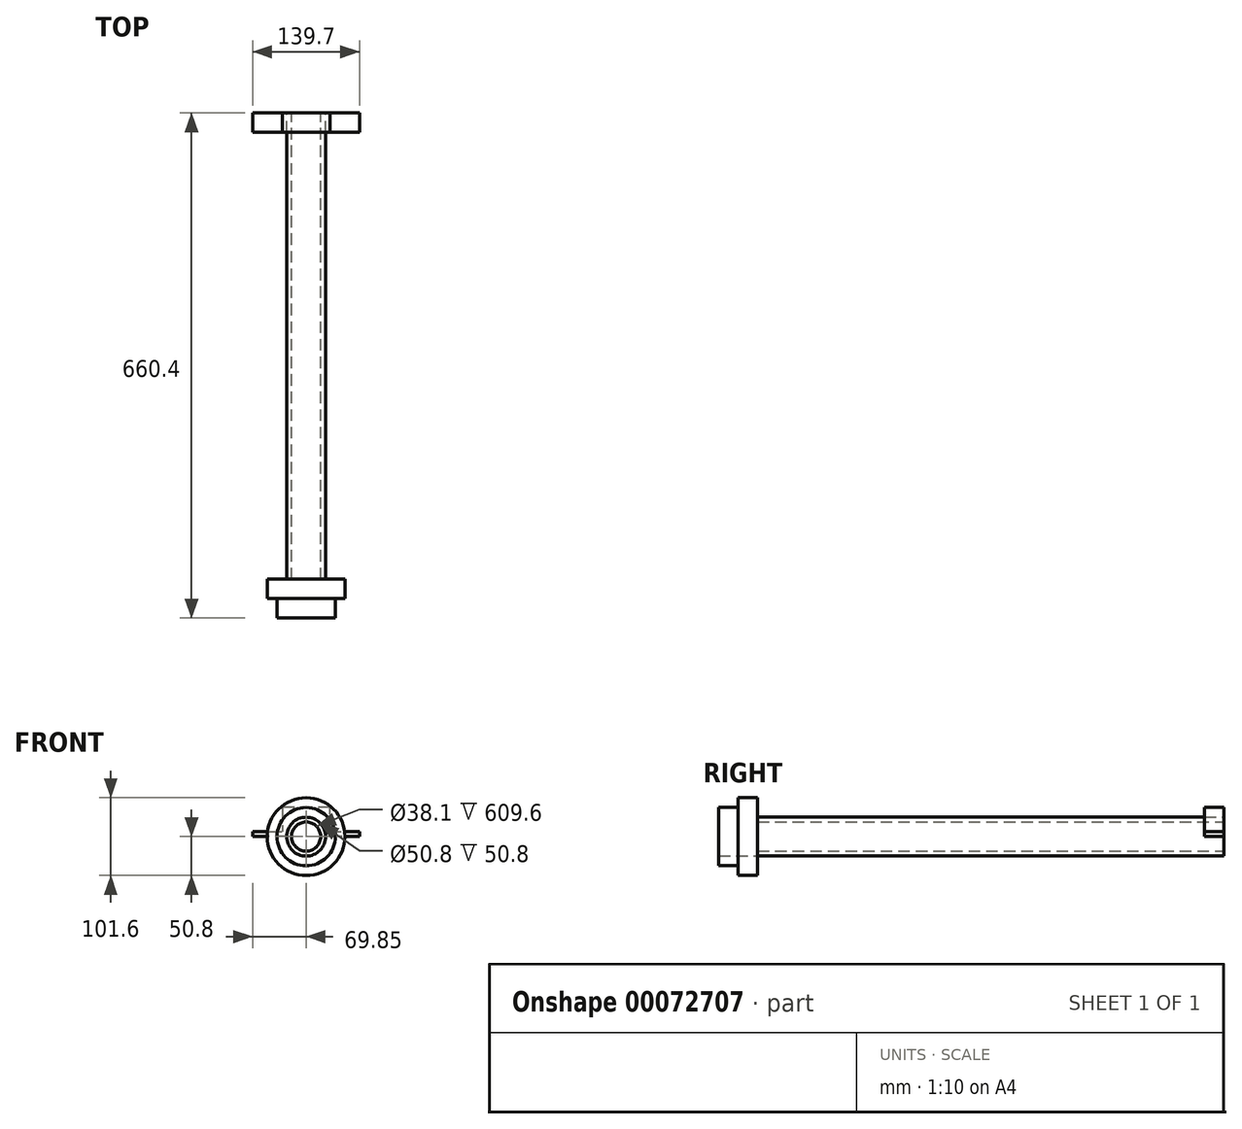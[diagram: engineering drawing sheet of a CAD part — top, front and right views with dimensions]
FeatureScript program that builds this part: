
annotation { "Feature Type Name" : "Feature", "Feature Type Description" : "" }
export const myFeature = defineFeature(function(context is Context, id is Id, definition is map)
    precondition{}
    {
        {
            var Q0;
            Q0=qCreatedBy(makeId("Front.planeOp"),FACE);
            var sketch = newSketch(context, id + "F0", { "sketchPlane" : qUnion([Q0])});
            skCircle(sketch, "E0", {"center": v(0, 0) * mm, "radius": 25.4 * mm});
            skCircle(sketch, "E1", {"center": v(0, 0) * mm, "radius": 19.05 * mm});
            skSolve(sketch);
        }
        {
            var Q0;
            Q0=makeQuery(id+"F0.imprint","IMPRINT",FACE,{"disambiguationData":[TD([[makeQuery(id+"F0.imprint","IMPRINT",EDGE,{"derivedFrom":sQuery(id+"F0.wireOp",EDGE,"E0")}),1.0]])]});
            extrude(context, id + "F1", {"entities" : qUnion([Q0]), "depth" : 609.6 * mm});
        }
        {
            var Q0;
            Q0=qCreatedBy(makeId("Front.planeOp"),FACE);
            var sketch = newSketch(context, id + "F2", { "sketchPlane" : qUnion([Q0])});
            skCircle(sketch, "E2.0", {"center": v(0, 0) * mm, "radius": 25.4 * mm});
            skLineSegment(sketch, "E3", {"start": v(69.85, 0) * mm, "end": v(-69.85, 0) * mm});
            skLineSegment(sketch, "E4", {"start": v(-69.85, 0) * mm, "end": v(-69.85, 6.35) * mm});
            skLineSegment(sketch, "E5", {"start": v(-69.85, 6.35) * mm, "end": v(-24.6, 6.35) * mm});
            skLineSegment(sketch, "E6", {"start": v(-24.6, 6.35) * mm, "end": v(24.6, 6.35) * mm});
            skLineSegment(sketch, "E7", {"start": v(24.6, 6.35) * mm, "end": v(69.85, 6.35) * mm});
            skLineSegment(sketch, "E8", {"start": v(69.85, 6.35) * mm, "end": v(69.85, 0) * mm});
            skCircle(sketch, "E9", {"center": v(0, 0) * mm, "radius": 31.75 * mm});
            skLineSegment(sketch, "E10.top", {"start": v(69.85, -6.35) * mm, "end": v(-69.85, -6.35) * mm});
            skLineSegment(sketch, "E10.left", {"start": v(69.85, 0) * mm, "end": v(69.85, -6.35) * mm});
            skLineSegment(sketch, "E10.right", {"start": v(-69.85, 0) * mm, "end": v(-69.85, -6.35) * mm});
            skSolve(sketch);
        }
        {
            var Q0;
            {var subQ1=sQuery(id+"F2.wireOp",EDGE,"E5");var subQ6=sQuery(id+"F2.wireOp",EDGE,"E9");var subQ7=makeQuery(id+"F2.imprint","INTERSECT",VERTEX,{"derivedFrom":[subQ1,subQ6]});Q0=makeQuery(id+"F2.imprint","IMPRINT",FACE,{"disambiguationData":[TD([[makeQuery(id+"F2.imprint","IMPRINT",EDGE,{"disambiguationData":[TD([[subQ7,1.0]])],"derivedFrom":subQ6}),1.0]])]});}
            var Q1;
            {var subQ0=sQuery(id+"F2.wireOp",EDGE,"E8");Q1=makeQuery(id+"F2.imprint","IMPRINT",FACE,{"disambiguationData":[TD([[makeQuery(id+"F2.imprint","IMPRINT",EDGE,{"derivedFrom":subQ0}),-1.0]])]});}
            var Q2;
            {var subQ0=sQuery(id+"F2.wireOp",EDGE,"E7");var subQ5=sQuery(id+"F2.wireOp",EDGE,"E9");var subQ6=makeQuery(id+"F2.imprint","INTERSECT",VERTEX,{"derivedFrom":[subQ0,subQ5]});Q2=makeQuery(id+"F2.imprint","IMPRINT",FACE,{"disambiguationData":[TD([[makeQuery(id+"F2.imprint","IMPRINT",EDGE,{"disambiguationData":[TD([[subQ6,1.0]])],"derivedFrom":subQ5}),1.0]])]});}
            var Q3;
            {var subQ0=sQuery(id+"F2.wireOp",EDGE,"E5");var subQ5=sQuery(id+"F2.wireOp",EDGE,"E9");var subQ6=makeQuery(id+"F2.imprint","INTERSECT",VERTEX,{"derivedFrom":[subQ0,subQ5]});Q3=makeQuery(id+"F2.imprint","IMPRINT",FACE,{"disambiguationData":[TD([[makeQuery(id+"F2.imprint","IMPRINT",EDGE,{"disambiguationData":[TD([[subQ6,-1.0]])],"derivedFrom":subQ5}),1.0]])]});}
            var Q4;
            {var subQ0=sQuery(id+"F2.wireOp",EDGE,"E4");Q4=makeQuery(id+"F2.imprint","IMPRINT",FACE,{"disambiguationData":[TD([[makeQuery(id+"F2.imprint","IMPRINT",EDGE,{"derivedFrom":subQ0}),-1.0]])]});}
            extrude(context, id + "F3", {"entities" : qUnion([Q0, Q1, Q2, Q3, Q4]), "depth" : 25.4 * mm});
        }
        {
            var Q0;
            Q0=qCreatedBy(makeId("Front.planeOp"),FACE);
            var sketch = newSketch(context, id + "F4", { "sketchPlane" : qUnion([Q0])});
            skArc(sketch, "E11.0", {"start": v(31.1, 6.35) * mm, "mid": v(0, 31.75) * mm, "end": v(-31.1, 6.35) * mm});
            skLineSegment(sketch, "E12", {"start": v(31.1, 6.35) * mm, "end": v(31.1, 31.75) * mm});
            skLineSegment(sketch, "E13", {"start": v(31.1, 31.75) * mm, "end": v(-31.1, 31.75) * mm});
            skLineSegment(sketch, "E14", {"start": v(-31.1, 31.75) * mm, "end": v(-31.1, 6.35) * mm});
            skLineSegment(sketch, "E15", {"start": v(31.1, 31.75) * mm, "end": v(31.1, 38.1) * mm});
            skLineSegment(sketch, "E16", {"start": v(31.1, 38.1) * mm, "end": v(-31.1, 38.1) * mm});
            skLineSegment(sketch, "E17", {"start": v(-31.1, 38.1) * mm, "end": v(-31.1, 31.75) * mm});
            skSolve(sketch);
        }
        {
            var Q0;
            {var subQ0=sQuery(id+"F4.wireOp",EDGE,"E15");Q0=makeQuery(id+"F4.imprint","IMPRINT",FACE,{"disambiguationData":[TD([[makeQuery(id+"F4.imprint","IMPRINT",EDGE,{"derivedFrom":subQ0}),1.0]])]});}
            var Q1;
            {var subQ0=sQuery(id+"F4.wireOp",EDGE,"E12");Q1=makeQuery(id+"F4.imprint","IMPRINT",FACE,{"disambiguationData":[TD([[makeQuery(id+"F4.imprint","IMPRINT",EDGE,{"derivedFrom":subQ0}),1.0]])]});}
            var Q2;
            {var subQ0=sQuery(id+"F4.wireOp",EDGE,"E14");Q2=makeQuery(id+"F4.imprint","IMPRINT",FACE,{"disambiguationData":[TD([[makeQuery(id+"F4.imprint","IMPRINT",EDGE,{"derivedFrom":subQ0}),1.0]])]});}
            extrude(context, id + "F5", {"entities" : qUnion([Q0, Q1, Q2]), "operationType" : NewBodyOperationType.ADD, "depth" : 25.4 * mm});
        }
        {
            var Q0;
            Q0=makeQuery(id+"F1.opExtrude","CAP_FACE",FACE,{"disambiguationData":[OSD([sQuery(id+"F0.wireOp",EDGE,"E0"),sQuery(id+"F0.wireOp",EDGE,"E1")])],"isStart":false});
            var sketch = newSketch(context, id + "F6", { "sketchPlane" : qUnion([Q0])});
            skCircle(sketch, "E18.0", {"center": v(0, 0) * mm, "radius": 25.4 * mm});
            skCircle(sketch, "E19", {"center": v(0, 0) * mm, "radius": 38.1 * mm});
            skCircle(sketch, "E20", {"center": v(0, 0) * mm, "radius": 50.8 * mm});
            skSolve(sketch);
        }
        {
            var Q0;
            Q0=makeQuery(id+"F6.imprint","IMPRINT",FACE,{"disambiguationData":[TD([[makeQuery(id+"F6.imprint","IMPRINT",EDGE,{"derivedFrom":sQuery(id+"F6.wireOp",EDGE,"E19")}),-1.0]])]});
            extrude(context, id + "F7", {"entities" : qUnion([Q0]), "depth" : 25.4 * mm});
        }
        {
            var Q0;
            Q0=makeQuery(id+"F6.imprint","IMPRINT",FACE,{"disambiguationData":[TD([[makeQuery(id+"F6.imprint","IMPRINT",EDGE,{"derivedFrom":sQuery(id+"F6.wireOp",EDGE,"E18.0")}),-1.0]])]});
            extrude(context, id + "F8", {"entities" : qUnion([Q0]), "operationType" : NewBodyOperationType.ADD, "depth" : 50.8 * mm});
        }
    });
